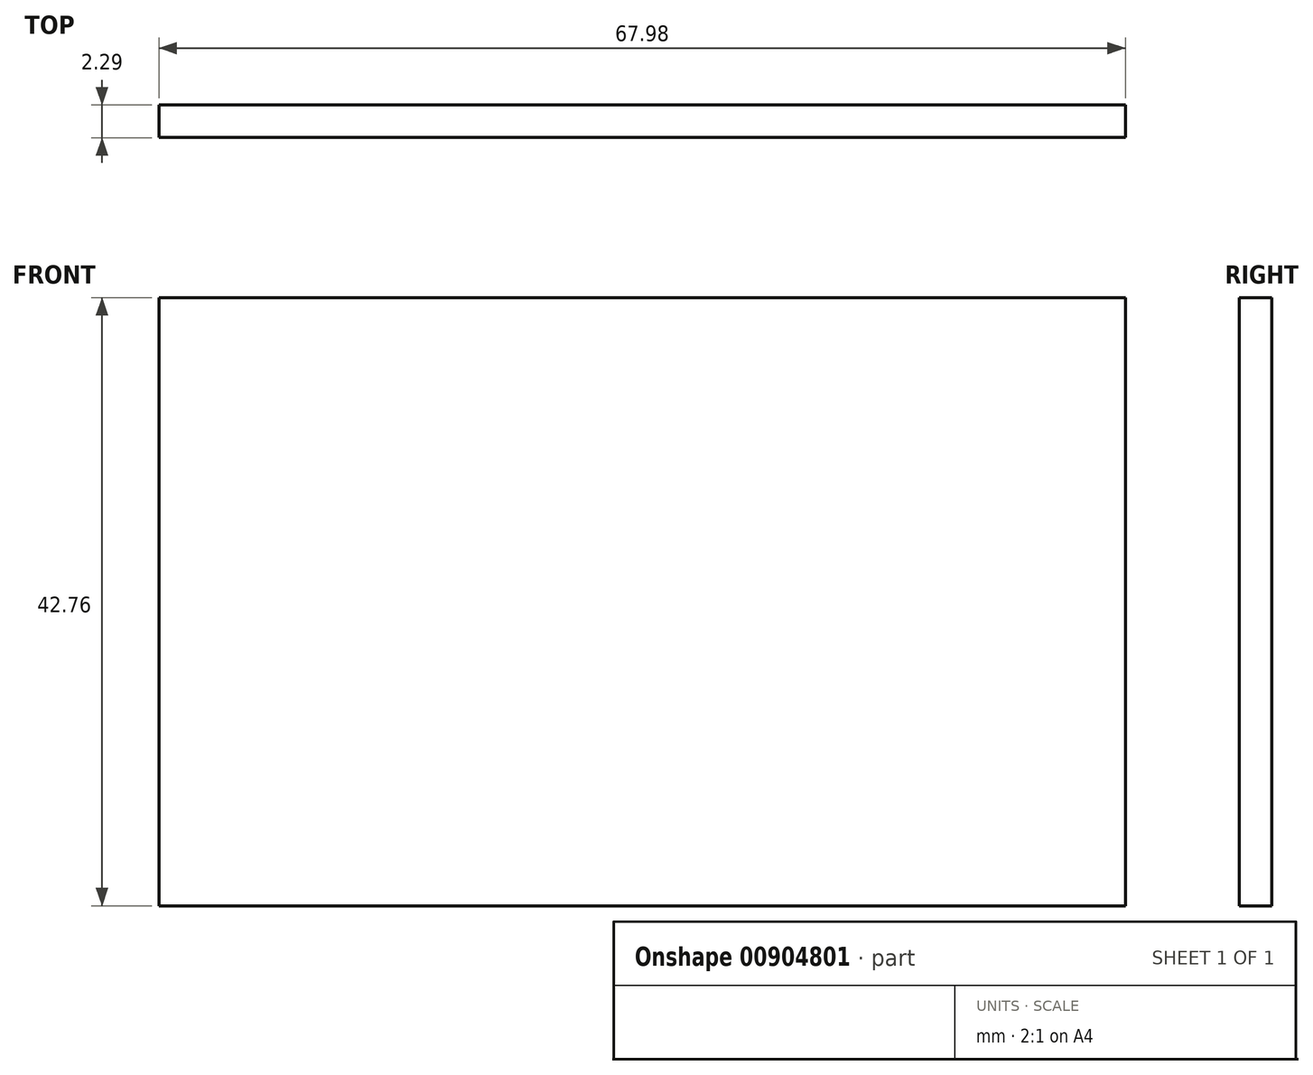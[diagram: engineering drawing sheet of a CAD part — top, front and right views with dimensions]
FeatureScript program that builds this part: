
annotation { "Feature Type Name" : "Feature", "Feature Type Description" : "" }
export const myFeature = defineFeature(function(context is Context, id is Id, definition is map)
    precondition{}
    {
        {
            var Q0;
            Q0=qCreatedBy(makeId("Front.planeOp"),FACE);
            var sketch = newSketch(context, id + "F0", { "sketchPlane" : qUnion([Q0])});
            skLineSegment(sketch, "E0.bottom", {"start": v(34, 21.38) * mm, "end": v(-34, 21.38) * mm});
            skLineSegment(sketch, "E0.top", {"start": v(34, -21.38) * mm, "end": v(-34, -21.38) * mm});
            skLineSegment(sketch, "E0.left", {"start": v(34, 21.38) * mm, "end": v(34, -21.38) * mm});
            skLineSegment(sketch, "E0.right", {"start": v(-34, 21.38) * mm, "end": v(-34, -21.38) * mm});
            skPoint(sketch, "E0.middle", {"position": v(0, 0) * mm});
            skSolve(sketch);
        }
        {
            var Q0;
            Q0=makeQuery(id+"F0.imprint","IMPRINT",FACE,{"disambiguationData":[TD([[makeQuery(id+"F0.imprint","IMPRINT",EDGE,{"derivedFrom":sQuery(id+"F0.wireOp",EDGE,"E0.bottom")}),1.0]])]});
            extrude(context, id + "F1", {"entities" : qUnion([Q0]), "depth" : 2.3 * mm, "offsetDistance" : 25.4 * mm});
        }
    });
